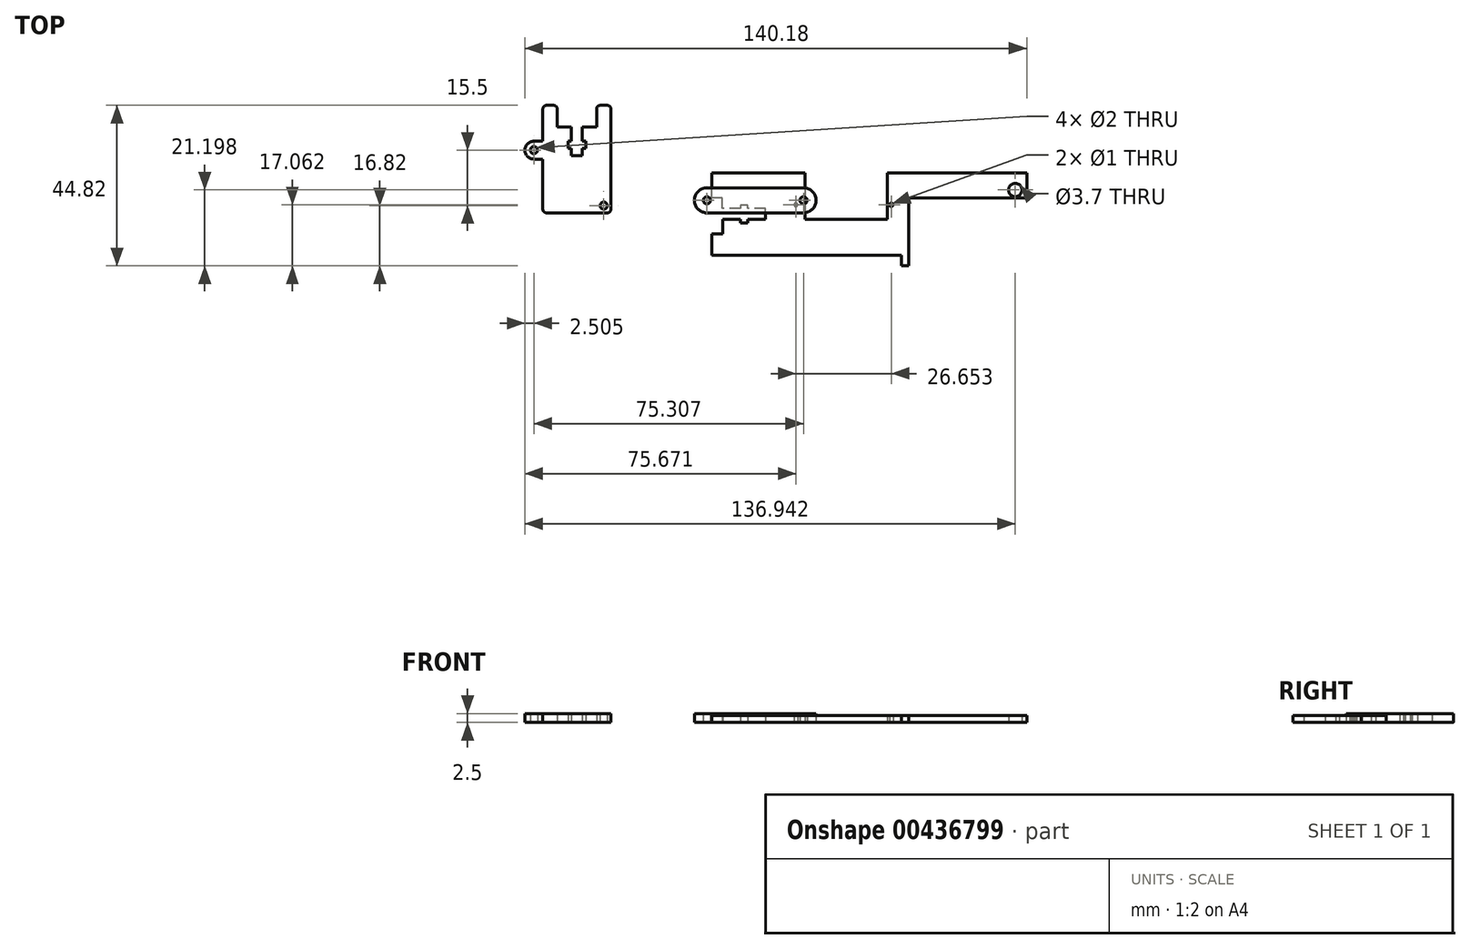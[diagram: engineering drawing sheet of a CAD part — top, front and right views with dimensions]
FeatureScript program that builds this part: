
annotation { "Feature Type Name" : "Feature", "Feature Type Description" : "" }
export const myFeature = defineFeature(function(context is Context, id is Id, definition is map)
    precondition{}
    {
        {
            var Q0;
            Q0=qCreatedBy(makeId("Top.planeOp"),FACE);
            var sketch = newSketch(context, id + "F0", { "sketchPlane" : qUnion([Q0])});
            skLineSegment(sketch, "E0", {"start": v(-63.45, 0) * mm, "end": v(-55.45, 0) * mm});
            skLineSegment(sketch, "E1", {"start": v(-54.45, 1) * mm, "end": v(-54.45, 29) * mm});
            skLineSegment(sketch, "E2", {"start": v(-55.45, 30) * mm, "end": v(-57.45, 30) * mm});
            skLineSegment(sketch, "E3", {"start": v(-58.45, 29) * mm, "end": v(-58.45, 24) * mm});
            skLineSegment(sketch, "E4", {"start": v(-58.45, 24) * mm, "end": v(-62.45, 24) * mm});
            skLineSegment(sketch, "E5", {"start": v(-62.45, 24) * mm, "end": v(-62.45, 20) * mm});
            skLineSegment(sketch, "E6", {"start": v(-62.45, 20) * mm, "end": v(-61.45, 20) * mm});
            skLineSegment(sketch, "E7", {"start": v(-61.45, 20) * mm, "end": v(-61.45, 18) * mm});
            skLineSegment(sketch, "E8", {"start": v(-61.45, 18) * mm, "end": v(-62.45, 18) * mm});
            skLineSegment(sketch, "E9", {"start": v(-62.45, 18) * mm, "end": v(-62.45, 16) * mm});
            skLineSegment(sketch, "E10", {"start": v(-62.45, 16) * mm, "end": v(-63.95, 16) * mm});
            skLineSegment(sketch, "E11", {"start": v(-63.95, 16) * mm, "end": v(-65.45, 16) * mm});
            skLineSegment(sketch, "E12", {"start": v(-65.45, 16) * mm, "end": v(-65.45, 18) * mm});
            skLineSegment(sketch, "E13", {"start": v(-65.45, 18) * mm, "end": v(-66.45, 18) * mm});
            skLineSegment(sketch, "E14", {"start": v(-66.45, 18) * mm, "end": v(-66.45, 20) * mm});
            skLineSegment(sketch, "E15", {"start": v(-66.45, 20) * mm, "end": v(-65.45, 20) * mm});
            skLineSegment(sketch, "E16", {"start": v(-65.45, 20) * mm, "end": v(-65.45, 24) * mm});
            skLineSegment(sketch, "E17", {"start": v(-65.45, 24) * mm, "end": v(-69.45, 24) * mm});
            skLineSegment(sketch, "E18", {"start": v(-69.45, 24) * mm, "end": v(-69.45, 29) * mm});
            skLineSegment(sketch, "E19", {"start": v(-70.45, 30) * mm, "end": v(-72.45, 30) * mm});
            skLineSegment(sketch, "E20", {"start": v(-73.45, 30) * mm, "end": v(-73.45, 1) * mm});
            skLineSegment(sketch, "E21", {"start": v(-72.45, 0) * mm, "end": v(-63.45, 0) * mm});
            skLineSegment(sketch, "E22", {"start": v(-73.45, 29) * mm, "end": v(-73.45, 20) * mm});
            skLineSegment(sketch, "E23", {"start": v(-73.45, 20) * mm, "end": v(-75.95, 20) * mm});
            skLineSegment(sketch, "E24", {"start": v(-78.45, 17.5) * mm, "end": v(-78.45, 17.5) * mm});
            skLineSegment(sketch, "E25", {"start": v(-75.95, 15) * mm, "end": v(-73.45, 15) * mm});
            skPoint(sketch, "E26.visualSharp", {"position": v(-54.45, 0) * mm});
            skArc(sketch, "E26.filletArc", {"start": v(-55.45, 0) * mm, "mid": v(-54.74, 0.3) * mm, "end": v(-54.45, 1) * mm});
            skPoint(sketch, "E27.visualSharp", {"position": v(-73.45, 0) * mm});
            skArc(sketch, "E27.filletArc", {"start": v(-73.45, 1) * mm, "mid": v(-73.15, 0.3) * mm, "end": v(-72.45, 0) * mm});
            skPoint(sketch, "E28.visualSharp", {"position": v(-73.45, 30) * mm});
            skArc(sketch, "E28.filletArc", {"start": v(-72.45, 30) * mm, "mid": v(-73.15, 29.7) * mm, "end": v(-73.45, 29) * mm});
            skPoint(sketch, "E29.visualSharp", {"position": v(-69.45, 30) * mm});
            skArc(sketch, "E29.filletArc", {"start": v(-69.45, 29) * mm, "mid": v(-69.74, 29.7) * mm, "end": v(-70.45, 30) * mm});
            skPoint(sketch, "E30.visualSharp", {"position": v(-58.45, 30) * mm});
            skArc(sketch, "E30.filletArc", {"start": v(-57.45, 30) * mm, "mid": v(-58.15, 29.7) * mm, "end": v(-58.45, 29) * mm});
            skPoint(sketch, "E31.visualSharp", {"position": v(-54.45, 30) * mm});
            skArc(sketch, "E31.filletArc", {"start": v(-54.45, 29) * mm, "mid": v(-54.74, 29.7) * mm, "end": v(-55.45, 30) * mm});
            skPoint(sketch, "E32.visualSharp", {"position": v(-78.45, 20) * mm});
            skArc(sketch, "E32.filletArc", {"start": v(-75.95, 20) * mm, "mid": v(-77.71, 19.27) * mm, "end": v(-78.45, 17.5) * mm});
            skPoint(sketch, "E33.visualSharp", {"position": v(-78.45, 15) * mm});
            skArc(sketch, "E33.filletArc", {"start": v(-78.45, 17.5) * mm, "mid": v(-77.71, 15.73) * mm, "end": v(-75.95, 15) * mm});
            skCircle(sketch, "E34", {"center": v(-75.95, 17.5) * mm, "radius": 1 * mm});
            skCircle(sketch, "E35", {"center": v(-56.45, 2) * mm, "radius": 1 * mm});
            skSolve(sketch);
        }
        {
            var Q0;
            Q0=makeQuery(id+"F0.imprint","IMPRINT",FACE,{"disambiguationData":[TD([[makeQuery(id+"F0.imprint","IMPRINT",EDGE,{"derivedFrom":sQuery(id+"F0.wireOp",EDGE,"E0")}),1.0]])]});
            extrude(context, id + "F1", {"entities" : qUnion([Q0]), "depth" : 2.5 * mm});
        }
        {
            var Q0;
            {var subQ0=sQuery(id+"F0.wireOp",EDGE,"E23");Q0=makeQuery(id+"F0.imprint","IMPRINT",FACE,{"disambiguationData":[TD([[makeQuery(id+"F0.imprint","IMPRINT",EDGE,{"derivedFrom":subQ0}),1.0]])]});}
            extrude(context, id + "F2", {"entities" : qUnion([Q0]), "operationType" : NewBodyOperationType.ADD, "depth" : 2.5 * mm});
        }
        {
            var Q0;
            Q0=qCreatedBy(makeId("Top.planeOp"),FACE);
            var sketch = newSketch(context, id + "F3", { "sketchPlane" : qUnion([Q0])});
            skLineSegment(sketch, "E36", {"start": v(-27.64, 0) * mm, "end": v(-0.64, 0) * mm});
            skLineSegment(sketch, "E37", {"start": v(2.86, 3.5) * mm, "end": v(2.86, 3.5) * mm});
            skLineSegment(sketch, "E38", {"start": v(-0.64, 7) * mm, "end": v(-27.64, 7) * mm});
            skLineSegment(sketch, "E39", {"start": v(-31.14, 3.5) * mm, "end": v(-31.14, 3.5) * mm});
            skPoint(sketch, "E40.visualSharp", {"position": v(2.86, 7) * mm});
            skArc(sketch, "E40.filletArc", {"start": v(2.86, 3.5) * mm, "mid": v(1.84, 5.97) * mm, "end": v(-0.64, 7) * mm});
            skPoint(sketch, "E41.visualSharp", {"position": v(2.86, 0) * mm});
            skArc(sketch, "E41.filletArc", {"start": v(-0.64, 0) * mm, "mid": v(1.84, 1.03) * mm, "end": v(2.86, 3.5) * mm});
            skPoint(sketch, "E42.visualSharp", {"position": v(-31.14, 0) * mm});
            skArc(sketch, "E42.filletArc", {"start": v(-31.14, 3.5) * mm, "mid": v(-30.11, 1.03) * mm, "end": v(-27.64, 0) * mm});
            skPoint(sketch, "E43.visualSharp", {"position": v(-31.14, 7) * mm});
            skArc(sketch, "E43.filletArc", {"start": v(-27.64, 7) * mm, "mid": v(-30.11, 5.97) * mm, "end": v(-31.14, 3.5) * mm});
            skCircle(sketch, "E44", {"center": v(-0.64, 3.5) * mm, "radius": 1 * mm});
            skCircle(sketch, "E45", {"center": v(-27.64, 3.5) * mm, "radius": 1 * mm});
            skSolve(sketch);
        }
        {
            var Q0;
            Q0=makeQuery(id+"F3.imprint","IMPRINT",FACE,{"disambiguationData":[TD([[makeQuery(id+"F3.imprint","IMPRINT",EDGE,{"derivedFrom":sQuery(id+"F3.wireOp",EDGE,"E36")}),1.0]])]});
            extrude(context, id + "F4", {"entities" : qUnion([Q0]), "depth" : 2.5 * mm});
        }
        {
            var Q0;
            Q0=qCreatedBy(makeId("Top.planeOp"),FACE);
            var sketch = newSketch(context, id + "F5", { "sketchPlane" : qUnion([Q0])});
            skLineSegment(sketch, "E46", {"start": v(-26.27, 11.18) * mm, "end": v(-0.27, 11.18) * mm});
            skLineSegment(sketch, "E47", {"start": v(-0.27, 11.18) * mm, "end": v(-0.27, -1.82) * mm});
            skLineSegment(sketch, "E48", {"start": v(-0.27, -1.82) * mm, "end": v(22.73, -1.82) * mm});
            skLineSegment(sketch, "E49", {"start": v(22.73, -1.82) * mm, "end": v(22.73, 11.18) * mm});
            skLineSegment(sketch, "E50", {"start": v(22.73, 11.18) * mm, "end": v(61.73, 11.18) * mm});
            skLineSegment(sketch, "E51", {"start": v(61.73, 11.18) * mm, "end": v(61.73, 4.18) * mm});
            skLineSegment(sketch, "E52", {"start": v(61.73, 4.18) * mm, "end": v(28.73, 4.18) * mm});
            skLineSegment(sketch, "E53", {"start": v(28.73, 4.18) * mm, "end": v(28.73, -14.82) * mm});
            skLineSegment(sketch, "E54", {"start": v(28.73, -14.82) * mm, "end": v(26.73, -14.82) * mm});
            skLineSegment(sketch, "E55", {"start": v(26.73, -14.82) * mm, "end": v(26.73, -11.82) * mm});
            skLineSegment(sketch, "E56", {"start": v(26.73, -11.82) * mm, "end": v(-26.27, -11.82) * mm});
            skLineSegment(sketch, "E57", {"start": v(-26.27, -11.82) * mm, "end": v(-26.27, -5.82) * mm});
            skLineSegment(sketch, "E58", {"start": v(-26.27, -5.82) * mm, "end": v(-23.27, -5.82) * mm});
            skLineSegment(sketch, "E59", {"start": v(-23.27, -5.82) * mm, "end": v(-23.27, -1.82) * mm});
            skLineSegment(sketch, "E60", {"start": v(-23.27, -1.82) * mm, "end": v(-18.27, -1.82) * mm});
            skLineSegment(sketch, "E61", {"start": v(-18.27, -1.82) * mm, "end": v(-18.27, -2.82) * mm});
            skLineSegment(sketch, "E62", {"start": v(-18.27, -2.82) * mm, "end": v(-16.27, -2.82) * mm});
            skLineSegment(sketch, "E63", {"start": v(-16.27, -2.82) * mm, "end": v(-16.27, -1.82) * mm});
            skLineSegment(sketch, "E64", {"start": v(-16.27, -1.82) * mm, "end": v(-11.27, -1.82) * mm});
            skLineSegment(sketch, "E65", {"start": v(-11.27, -1.82) * mm, "end": v(-11.27, 1.18) * mm});
            skLineSegment(sketch, "E66", {"start": v(-11.27, 1.18) * mm, "end": v(-16.27, 1.18) * mm});
            skLineSegment(sketch, "E67", {"start": v(-16.27, 1.18) * mm, "end": v(-16.27, 2.18) * mm});
            skLineSegment(sketch, "E68", {"start": v(-16.27, 2.18) * mm, "end": v(-18.27, 2.18) * mm});
            skLineSegment(sketch, "E69", {"start": v(-18.27, 2.18) * mm, "end": v(-18.27, 1.18) * mm});
            skLineSegment(sketch, "E70", {"start": v(-18.27, 1.18) * mm, "end": v(-23.3, 1.18) * mm});
            skLineSegment(sketch, "E71", {"start": v(-23.3, 1.18) * mm, "end": v(-23.3, 4.18) * mm});
            skLineSegment(sketch, "E72", {"start": v(-23.3, 4.18) * mm, "end": v(-26.23, 4.18) * mm});
            skLineSegment(sketch, "E73", {"start": v(-26.23, 4.18) * mm, "end": v(-26.27, 11.18) * mm});
            skCircle(sketch, "E74", {"center": v(58.5, 6.38) * mm, "radius": 1.85 * mm});
            skCircle(sketch, "E75", {"center": v(23.87, 2.24) * mm, "radius": 0.5 * mm});
            skCircle(sketch, "E76", {"center": v(-2.78, 2.24) * mm, "radius": 0.5 * mm});
            skSolve(sketch);
        }
        {
            var Q0;
            Q0 = qSketchRegion(id + "F5", true);
            extrude(context, id + "F6", {"entities" : qUnion([Q0]), "depth" : 2 * mm});
        }
    });
